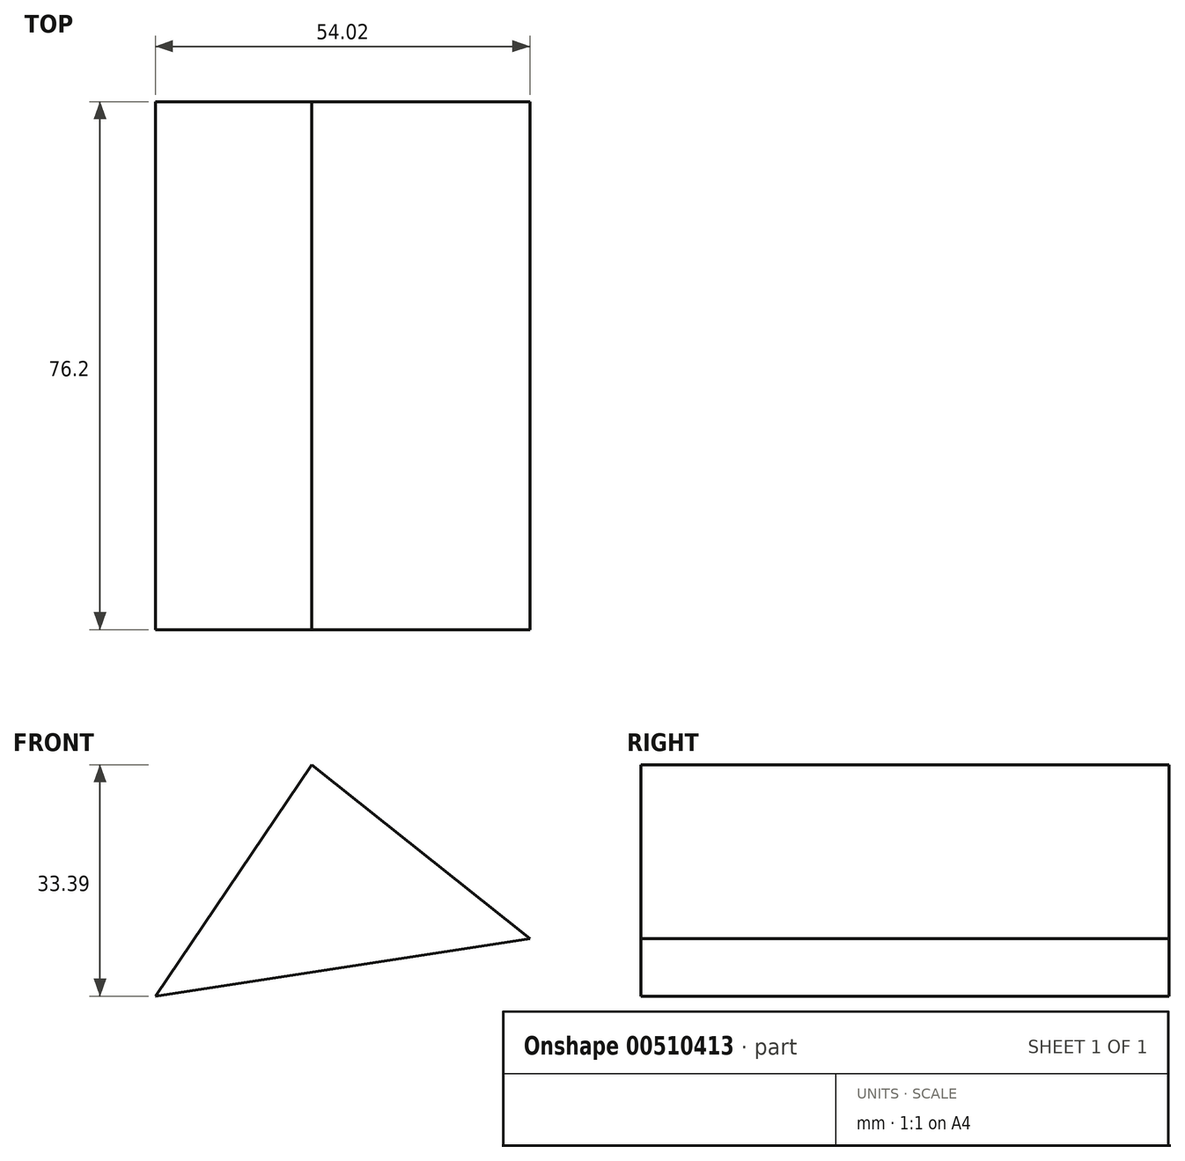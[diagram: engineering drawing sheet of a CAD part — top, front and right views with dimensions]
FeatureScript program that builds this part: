
annotation { "Feature Type Name" : "Feature", "Feature Type Description" : "" }
export const myFeature = defineFeature(function(context is Context, id is Id, definition is map)
    precondition{}
    {
        {
            var Q0;
            Q0=qCreatedBy(makeId("Front.planeOp"),FACE);
            var sketch = newSketch(context, id + "F0", { "sketchPlane" : qUnion([Q0])});
            skLineSegment(sketch, "E0", {"start": v(-31.84, -6.19) * mm, "end": v(-9.32, 27.2) * mm});
            skLineSegment(sketch, "E1", {"start": v(-9.32, 27.2) * mm, "end": v(22.18, 2.1) * mm});
            skLineSegment(sketch, "E2", {"start": v(-31.84, -6.19) * mm, "end": v(22.18, 2.1) * mm});
            skSolve(sketch);
        }
        {
            var Q0;
            Q0=makeQuery(id+"F0.imprint","IMPRINT",FACE,{"disambiguationData":[TD([[makeQuery(id+"F0.imprint","IMPRINT",EDGE,{"derivedFrom":sQuery(id+"F0.wireOp",EDGE,"E0")}),-1.0]])]});
            extrude(context, id + "F1", {"entities" : qUnion([Q0]), "depth" : 76.2 * mm});
        }
    });
